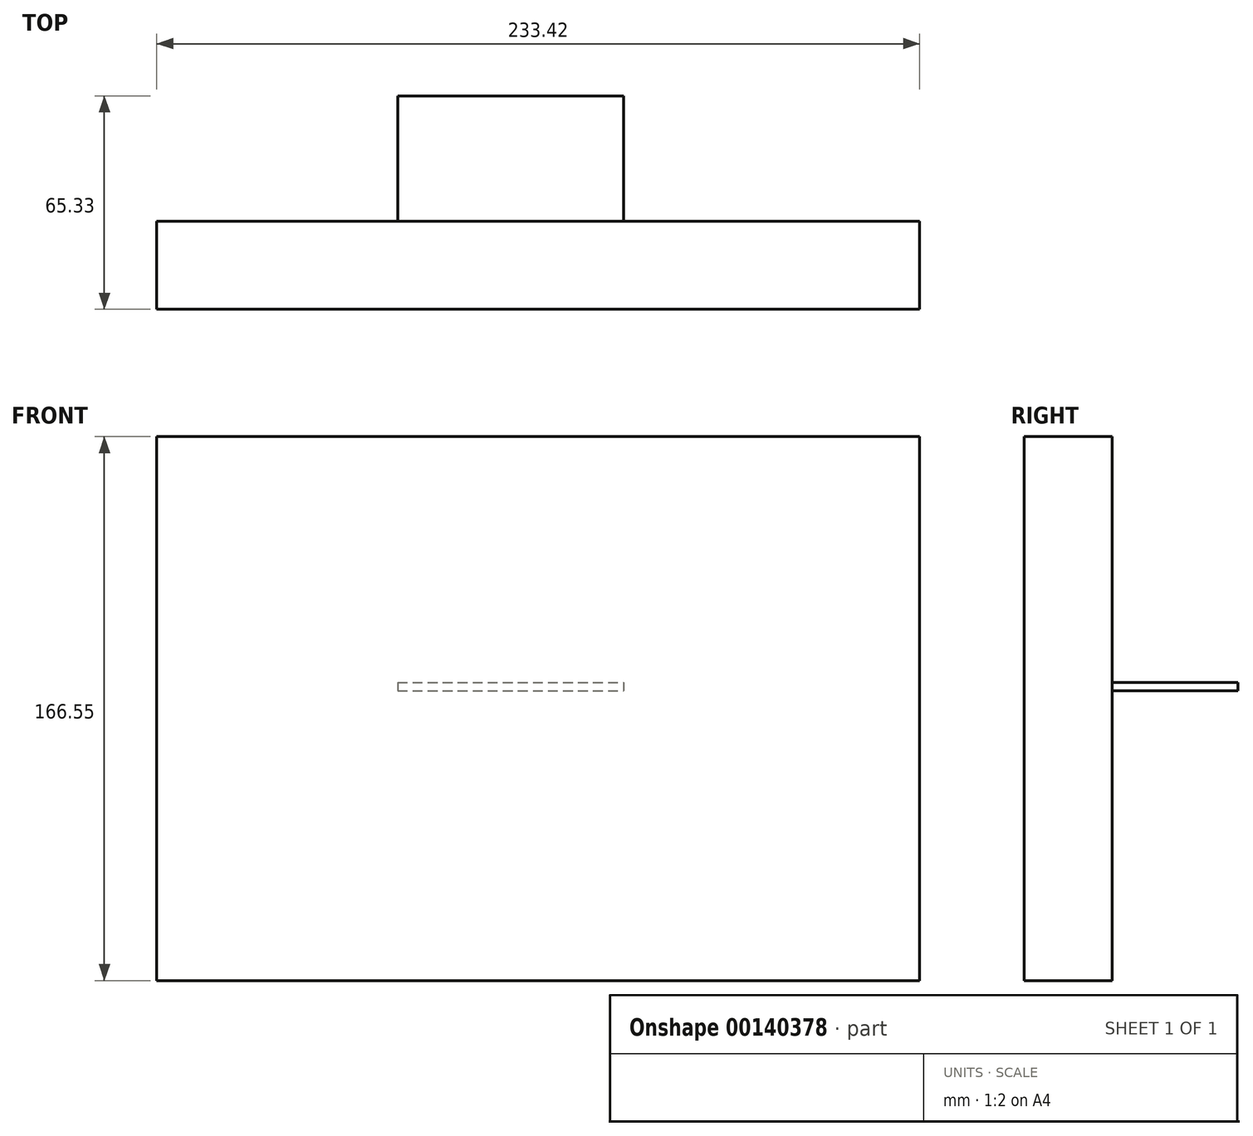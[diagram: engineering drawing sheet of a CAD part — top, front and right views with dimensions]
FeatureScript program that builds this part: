
annotation { "Feature Type Name" : "Feature", "Feature Type Description" : "" }
export const myFeature = defineFeature(function(context is Context, id is Id, definition is map)
    precondition{}
    {
        {
            var Q0;
            Q0=qCreatedBy(makeId("Front.planeOp"),FACE);
            var sketch = newSketch(context, id + "F0", { "sketchPlane" : qUnion([Q0])});
            skLineSegment(sketch, "E0.bottom", {"start": v(-115.06, -88.76) * mm, "end": v(118.36, -88.76) * mm});
            skLineSegment(sketch, "E0.top", {"start": v(-115.06, 77.79) * mm, "end": v(118.36, 77.79) * mm});
            skLineSegment(sketch, "E0.left", {"start": v(-115.06, -88.76) * mm, "end": v(-115.06, 77.79) * mm});
            skLineSegment(sketch, "E0.right", {"start": v(118.36, -88.76) * mm, "end": v(118.36, 77.79) * mm});
            skSolve(sketch);
        }
        {
            var Q0;
            Q0=makeQuery(id+"F0.imprint","IMPRINT",FACE,{"disambiguationData":[TD([[makeQuery(id+"F0.imprint","IMPRINT",EDGE,{"derivedFrom":sQuery(id+"F0.wireOp",EDGE,"E0.bottom")}),1.0]])]});
            extrude(context, id + "F1", {"entities" : qUnion([Q0]), "depth" : 1.27 * mm});
        }
        {
            var Q0;
            Q0=makeQuery(id+"F1.opExtrude","CAP_FACE",FACE,{"disambiguationData":[OSD([sQuery(id+"F0.wireOp",EDGE,"E0.bottom"),sQuery(id+"F0.wireOp",EDGE,"E0.top"),sQuery(id+"F0.wireOp",EDGE,"E0.left"),sQuery(id+"F0.wireOp",EDGE,"E0.right")])],"isStart":false});
            extrude(context, id + "F2", {"entities" : qUnion([Q0]), "operationType" : NewBodyOperationType.ADD, "depth" : 0.25 * mm});
        }
        {
            var Q0;
            Q0=makeQuery(id+"F2.opExtrude","CAP_FACE",FACE,{"disambiguationData":[OSD([sQuery(id+"F0.wireOp",EDGE,"E0.bottom"),sQuery(id+"F0.wireOp",EDGE,"E0.top"),sQuery(id+"F0.wireOp",EDGE,"E0.left"),sQuery(id+"F0.wireOp",EDGE,"E0.right")])],"isStart":false});
            extrude(context, id + "F3", {"entities" : qUnion([Q0]), "operationType" : NewBodyOperationType.ADD, "depth" : 25.4 * mm});
        }
        {
            var Q0;
            Q0=qCreatedBy(makeId("Top.planeOp"),FACE);
            var sketch = newSketch(context, id + "F4", { "sketchPlane" : qUnion([Q0])});
            skLineSegment(sketch, "E1.bottom", {"start": v(-41.37, 0) * mm, "end": v(27.73, 0) * mm});
            skLineSegment(sketch, "E1.top", {"start": v(-41.37, 38.4) * mm, "end": v(27.73, 38.4) * mm});
            skLineSegment(sketch, "E1.left", {"start": v(-41.37, 0) * mm, "end": v(-41.37, 38.4) * mm});
            skLineSegment(sketch, "E1.right", {"start": v(27.73, 0) * mm, "end": v(27.73, 38.4) * mm});
            skSolve(sketch);
        }
        {
            var Q0;
            Q0=makeQuery(id+"F4.imprint","IMPRINT",FACE,{"disambiguationData":[TD([[makeQuery(id+"F4.imprint","IMPRINT",EDGE,{"derivedFrom":sQuery(id+"F4.wireOp",EDGE,"E1.bottom")}),1.0]])]});
            extrude(context, id + "F5", {"entities" : qUnion([Q0]), "operationType" : NewBodyOperationType.ADD, "depth" : 2.54 * mm});
        }
    });
